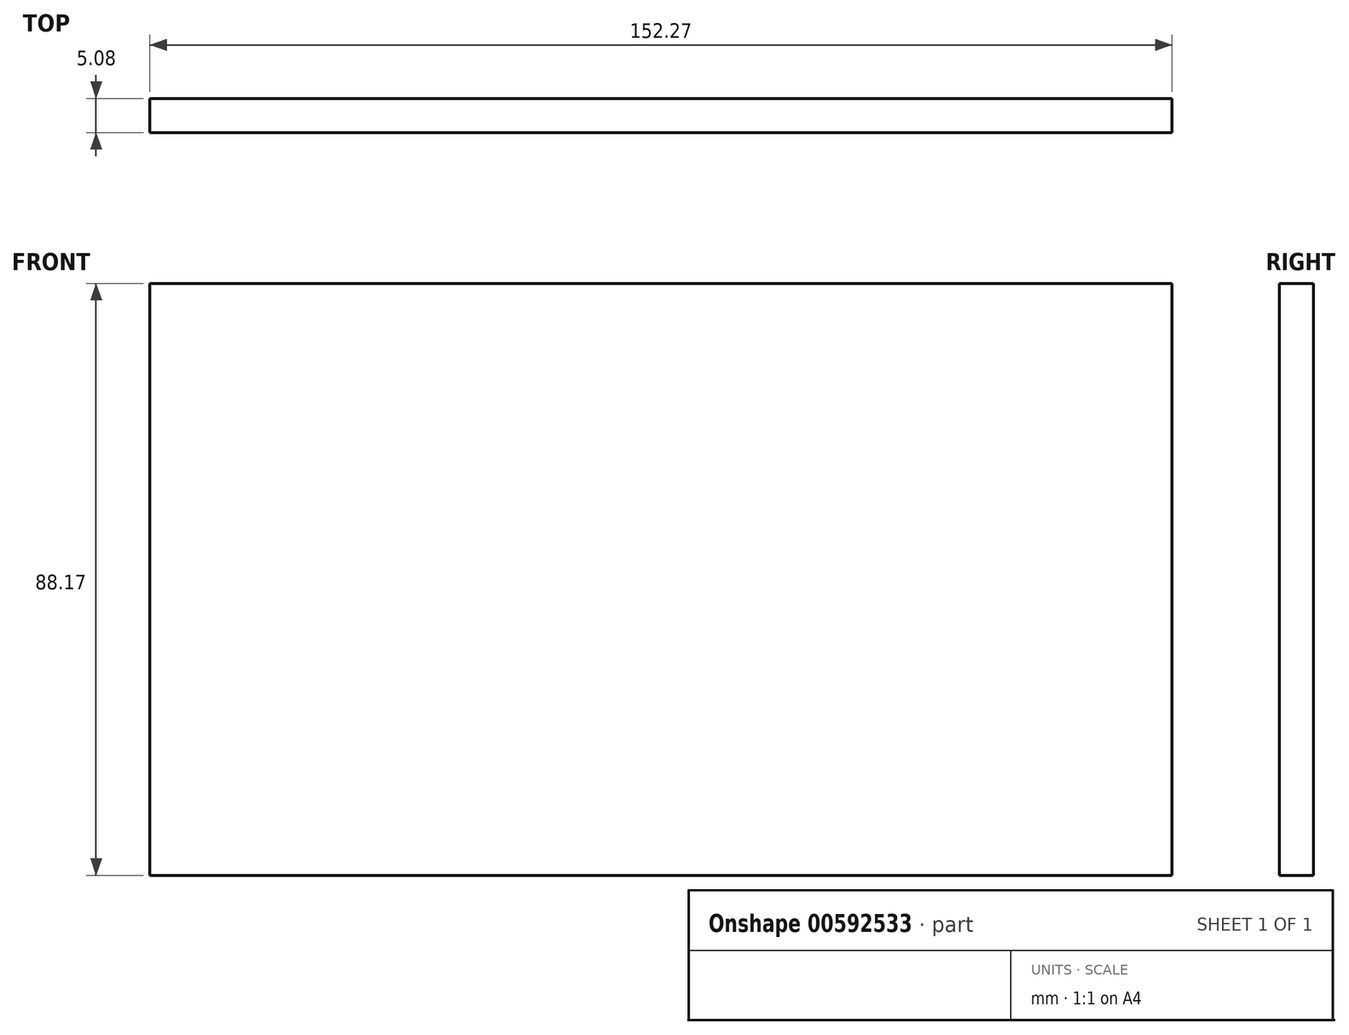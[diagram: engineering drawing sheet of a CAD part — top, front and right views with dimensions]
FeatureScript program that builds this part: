
annotation { "Feature Type Name" : "Feature", "Feature Type Description" : "" }
export const myFeature = defineFeature(function(context is Context, id is Id, definition is map)
    precondition{}
    {
        {
            var Q0;
            Q0=qCreatedBy(makeId("Front.planeOp"),FACE);
            var sketch = newSketch(context, id + "F0", { "sketchPlane" : qUnion([Q0])});
            skLineSegment(sketch, "E0.bottom", {"start": v(-75.93, -76.34) * mm, "end": v(76.34, -76.34) * mm});
            skLineSegment(sketch, "E0.top", {"start": v(-75.93, 11.83) * mm, "end": v(76.34, 11.83) * mm});
            skLineSegment(sketch, "E0.left", {"start": v(-75.93, -76.34) * mm, "end": v(-75.93, 11.83) * mm});
            skLineSegment(sketch, "E0.right", {"start": v(76.34, -76.34) * mm, "end": v(76.34, 11.83) * mm});
            skSolve(sketch);
        }
        {
            var Q0;
            Q0 = qSketchRegion(id + "F0", true);
            extrude(context, id + "F1", {"entities" : qUnion([Q0]), "depth" : 5.08 * mm, "offsetDistance" : 25.4 * mm});
        }
    });
